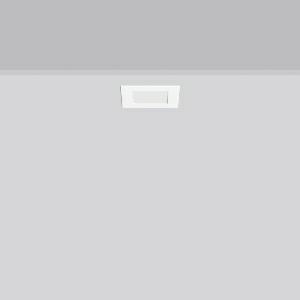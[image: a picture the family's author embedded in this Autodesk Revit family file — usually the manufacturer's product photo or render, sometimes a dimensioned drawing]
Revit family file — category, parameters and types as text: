
# Revit family: toledo_flat_square_e_672241_002_1_b32b
name_source: partatom
category: Lighting Fixtures
units: mm (PartAtom-declared; Revit-internal decimal feet)

## family parameters
Cut with Voids When Loaded = No
Host = Face
Light Source = No
Part Type = Normal
Room Calculation Point = No
Round Connector Dimension = Use Diameter
Shared = No

## types (1)
- TOLEDO FLAT square E (1 x LED Modul 840, 380 lm, 4000)
    Apparent Load = 5 VA
    CIE Flux Codes = 49 80 96 100 100
    Color Rendering = 80
    Color Temperature = 4000
    Default Elevation = 1800 mm
    Description = Series: TOLEDO FLAT square
Square recessed downlight. For escape route illumination. Housing: die-cast aluminium, powder-coated. Lightguide and diffuser made of non-yellowing plastic (PMMA). Diffuser opal matt plastic. Ceiling installation with spring system. Including separate LED converter with connecting cable 250 mm. Suitable for connection to central battery systems. External driver with simple plug-in locking system. 
Colour: white
Length: 110 mm
Width: 110 mm
Height: 3 mm
Cut-out length: 96 mm
Cut-out width: 96 mm
Recess height: 40 mm
Luminaire: recess height: 31-51 mm
Weight: 243 g
Operating mode: maintained power mode
Lamp: LED
Socket: without socket
Colour temperature: 4000K
Colour rendering index (CRI): 80
System power: 4.7 W
Rated luminous flux: 380 lm
Luminous flux, emergency: 380 lm
System power, emergency: 4.7 W
Control gear: Regulated power supply
Protection class: II
Type of protection: IP 54
    Height = 0 mm  [stored 0 ft]
    Lamp = 1 x LED Modul 840
    Lamp Light Flux = 380 lm
    Lamp count = 1
    Length = 110 mm
    Lifetime = 50000 h
    Luminous efficacy = 81 lm/W
    Manufacturer = RZB
    ModVariant = No
    Model = 672241.002.1
    Mounting Place = Ceiling
    Mounting Type = Recessed
    Number of Poles = 1
    OnlyDefault = Yes
    Power Factor = 1
    Product Name = TOLEDO FLAT square E
    Product group = Recessed downlights
    ProductGroupID = 402
    Protection Class = Protection class II
    Protection Degree = IP 40
    RLX_Detail_Level = 1
    RLX_Emergency_Light_Flux = 380 lm
    RLX_Emergency_Type = 3
    RLX_Emergency_Type_DB = Yes
    RlxData = <blob elided: 9673 chars, md5=621d21f2>
    Socket = socket
    Standby Power = 0 W
    System Light Flux = 380 lm
    System Power = 5 W
    Type Comments = Product without accessories
    Type Image = 901485.002.jpg
    URL = http://relux.com
    VarID = ---
    Voltage = 230 V
    Voltage Range = 220-240 V
    Weight = 0.00 kg
    Width = 110 mm

note: [stored X ft] marks values corroborated as IEEE doubles in the binary element streams (Revit-internal decimal feet)

## geometry (parser evidence)
native form markers: Sweep x9
no freeform markers — native parametric forms only
